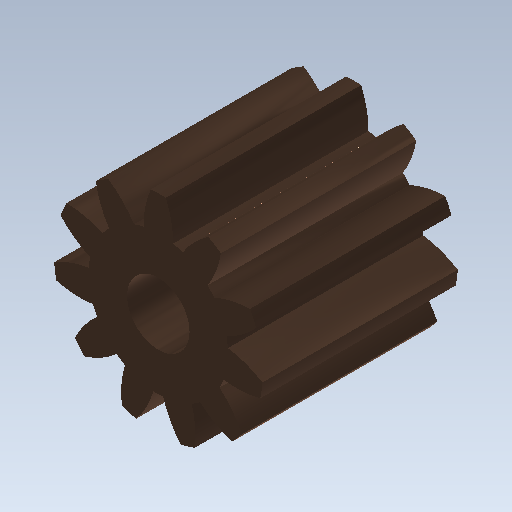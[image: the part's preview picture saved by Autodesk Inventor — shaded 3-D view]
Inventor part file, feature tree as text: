
AUTODESK INVENTOR PART (.ipt)
format: ipt  version: 2020 (Build 240168000, 168)  size: 224,768 bytes
history: native  units: mm (DEFAULTED — no unit token found)
features: plane x3, other x3, sketch x3, extrude x1, hole x1
ambient origin geometry x8: Origin, YZ Plane, XZ Plane, XY Plane, X Axis, Y Axis, Z Axis, Center Point
bodies: Solid1 (feature_tree)
feature tree (11):
  extrude  "Extrusion1"  Depth=2.5mm TaperAngle=0.0deg
  plane  "Work Plane2"
  plane  "Work Plane8"
  plane  "Work Plane9"
  other  "Цилиндрическое зубчатое зацепление"
  hole  "Отверстие1"  [1 undecoded]
  sketch  "Sketch1"  dims[d0=2.6719mm d1=2.5mm d2=0.0mm]
  sketch  "Sketch2"  dims[d3=2.237288mm d4=10.0mm d5=0.0mm d16=6.0mm d17=0.0mm d34=2.855993mm d39=0.0mm d41=0.0mm d43=6.0mm d46=6.0mm d47=0.0mm d48=0.0mm d49=0.8mm d50=6.0mm d51=4.0mm d52=2.0mm d53=90.0deg d54=8.0mm d55=20.594885mm]
  other  "Srf1"
  sketch  "Эскиз3"
  other  "Средний диаметр"
note: 1 required parameter value undecoded (feature->parameter linkage not recoverable at this tier; creation-order binding heuristic only, values carry confidence <= 0.55)
